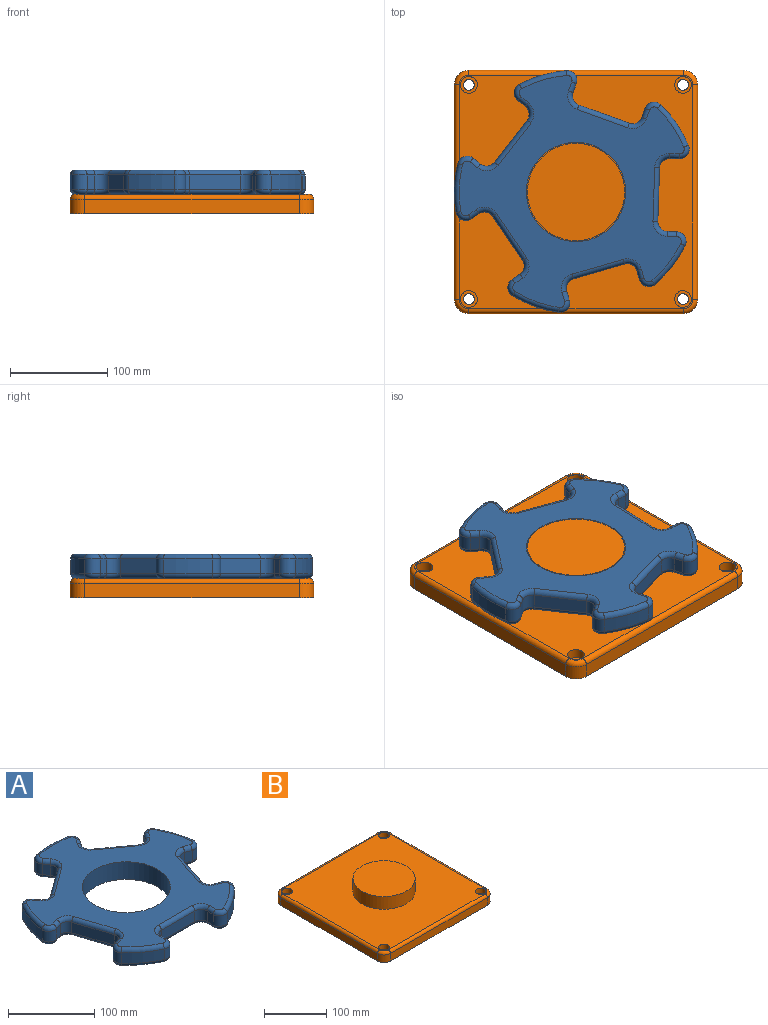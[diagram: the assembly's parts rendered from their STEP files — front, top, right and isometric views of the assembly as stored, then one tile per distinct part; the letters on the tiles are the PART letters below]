
ASSEMBLY  parts=2 mates=1
PART A: 123 faces, bbox 268.9x258.5x25 mm
  f0: plane 238.57x229.73mm, normal (0,0,1), area 21505.7mm2, adj f6,f43,f44,f45,f46,f47,f48,f49
  f1: plane 238.57x229.73mm, normal (0,0,-1), area 21505.7mm2, adj f6,f83,f84,f85,f86,f87,f88,f89
  f2: cylinder r=125mm len=40.68mm, axis (0,0,-1), area 759.5mm2, adj f13,f42,f51,f91
  f3: cylinder r=125mm len=47.82mm, axis (0,0,-1), area 759.5mm2, adj f35,f41,f67,f107
  f4: cylinder r=125mm len=50.29mm, axis (0,0,-1), area 759.5mm2, adj f28,f34,f82,f122
  f5: cylinder r=125mm len=47.82mm, axis (0,0,-1), area 759.5mm2, adj f21,f27,f66,f106
  f6: cylinder r=51mm len=102mm, axis (0,0,-1), area 8011.1mm2, adj f0,f1
  f7: cylinder r=125mm len=40.68mm, axis (0,0,-1), area 759.5mm2, adj f14,f20,f50,f90
  f8: plane 15x9.73mm, normal (-1,0,0), area 146mm2, adj f11,f14,f46,f86
  f9: plane 55x15mm, normal (0,-1,0), area 825mm2, adj f11,f12,f43,f83
  f10: plane 15x9.73mm, normal (1,0,0), area 146mm2, adj f12,f13,f47,f87
  f11: cylinder r=10mm len=15mm, axis (0,0,-1), area 235.6mm2, adj f8,f9,f44,f84
  f12: cylinder r=10mm len=15mm, axis (0,0,-1), area 235.6mm2, adj f9,f10,f45,f85
  f13: cylinder r=10mm len=15mm, axis (0,0,-1), area 299.5mm2, adj f2,f10,f49,f89
  f14: cylinder r=10mm len=15mm, axis (0,0,-1), area 299.5mm2, adj f7,f8,f48,f88
  f15: plane 15x9.26mm, normal (-0.31,-0.95,0), area 146mm2, adj f18,f21,f62,f102
  f16: plane 52.31x17mm, normal (0.95,-0.31,0), area 825mm2, adj f18,f19,f58,f98
  f17: plane 15x9.26mm, normal (0.31,0.95,0), area 146mm2, adj f19,f20,f54,f94
  f18: cylinder r=10mm len=15mm, axis (0,0,-1), area 235.6mm2, adj f15,f16,f60,f100
  f19: cylinder r=10mm len=15mm, axis (0,0,-1), area 235.6mm2, adj f16,f17,f56,f96
  f20: cylinder r=10mm len=16.25mm, axis (0,0,-1), area 299.5mm2, adj f7,f17,f52,f92
  f21: cylinder r=10mm len=15mm, axis (0,0,-1), area 299.5mm2, adj f5,f15,f64,f104
  f22: plane 15x7.87mm, normal (0.81,-0.59,0), area 146mm2, adj f25,f28,f78,f118
  f23: plane 44.5x32.33mm, normal (0.59,0.81,0), area 825mm2, adj f25,f26,f74,f114
  f24: plane 15x7.87mm, normal (-0.81,0.59,0), area 146mm2, adj f26,f27,f70,f110
  f25: cylinder r=10mm len=15mm, axis (0,0,-1), area 235.6mm2, adj f22,f23,f76,f116
  f26: cylinder r=10mm len=15mm, axis (0,0,-1), area 235.6mm2, adj f23,f24,f72,f112
  f27: cylinder r=10mm len=16.78mm, axis (0,0,-1), area 299.5mm2, adj f5,f24,f68,f108
  f28: cylinder r=10mm len=15.67mm, axis (0,0,-1), area 299.5mm2, adj f4,f22,f80,f120
  f29: plane 15x7.87mm, normal (0.81,0.59,0), area 146mm2, adj f32,f35,f71,f111
  f30: plane 44.5x32.33mm, normal (-0.59,0.81,0), area 825mm2, adj f32,f33,f75,f115
  f31: plane 15x7.87mm, normal (-0.81,-0.59,0), area 146mm2, adj f33,f34,f79,f119
  f32: cylinder r=10mm len=15mm, axis (0,0,-1), area 235.6mm2, adj f29,f30,f73,f113
  f33: cylinder r=10mm len=15mm, axis (0,0,-1), area 235.6mm2, adj f30,f31,f77,f117
  f34: cylinder r=10mm len=15.67mm, axis (0,0,-1), area 299.5mm2, adj f4,f31,f81,f121
  f35: cylinder r=10mm len=16.78mm, axis (0,0,-1), area 299.5mm2, adj f3,f29,f69,f109
  f36: plane 15x9.26mm, normal (-0.31,0.95,0), area 146mm2, adj f39,f42,f55,f95
  f37: plane 52.31x17mm, normal (-0.95,-0.31,0), area 825mm2, adj f39,f40,f59,f99
  f38: plane 15x9.26mm, normal (0.31,-0.95,0), area 146mm2, adj f40,f41,f63,f103
  f39: cylinder r=10mm len=15mm, axis (0,0,-1), area 235.6mm2, adj f36,f37,f57,f97
  f40: cylinder r=10mm len=15mm, axis (0,0,-1), area 235.6mm2, adj f37,f38,f61,f101
  f41: cylinder r=10mm len=15mm, axis (0,0,-1), area 299.5mm2, adj f3,f38,f65,f105
  f42: cylinder r=10mm len=16.25mm, axis (0,0,-1), area 299.5mm2, adj f2,f36,f53,f93
  f43: cylinder r=5mm len=55mm, axis (1,0,0), area 432mm2, adj f0,f9,f44,f45
  f44: torus R=15mm, axis (0,0,1), area 145.8mm2, adj f0,f11,f43,f46
  f45: torus R=15mm, axis (0,0,1), area 145.8mm2, adj f0,f12,f43,f47
  f46: cylinder r=5mm len=9.73mm, axis (0,-1,0), area 76.4mm2, adj f0,f8,f44,f48
  f47: cylinder r=5mm len=9.73mm, axis (0,1,0), area 76.4mm2, adj f0,f10,f45,f49
  f48: torus R=5mm, axis (0,0,1), area 128.3mm2, adj f0,f14,f46,f50
  f49: torus R=5mm, axis (0,0,1), area 128.3mm2, adj f0,f13,f47,f51
  f50: torus R=120mm, axis (0,0,1), area 391.9mm2, adj f0,f7,f48,f52
  f51: torus R=120mm, axis (0,0,1), area 391.9mm2, adj f0,f2,f49,f53
  f52: torus R=5mm, axis (0,0,1), area 128.3mm2, adj f0,f20,f50,f54
  f53: torus R=5mm, axis (0,0,1), area 128.3mm2, adj f0,f42,f51,f55
  f54: cylinder r=5mm len=10.8mm, axis (-0.95,0.31,0), area 76.4mm2, adj f0,f17,f52,f56
  f55: cylinder r=5mm len=10.8mm, axis (-0.95,-0.31,0), area 76.4mm2, adj f0,f36,f53,f57
  f56: torus R=15mm, axis (0,0,1), area 145.8mm2, adj f0,f19,f54,f58
  f57: torus R=15mm, axis (0,0,1), area 145.8mm2, adj f0,f39,f55,f59
  f58: cylinder r=5mm len=53.85mm, axis (0.31,0.95,0), area 432mm2, adj f0,f16,f56,f60
  f59: cylinder r=5mm len=53.85mm, axis (0.31,-0.95,0), area 432mm2, adj f0,f37,f57,f61
  f60: torus R=15mm, axis (0,0,1), area 145.8mm2, adj f0,f18,f58,f62
  f61: torus R=15mm, axis (0,0,1), area 145.8mm2, adj f0,f40,f59,f63
  f62: cylinder r=5mm len=10.8mm, axis (0.95,-0.31,0), area 76.4mm2, adj f0,f15,f60,f64
  f63: cylinder r=5mm len=10.8mm, axis (0.95,0.31,0), area 76.4mm2, adj f0,f38,f61,f65
  f64: torus R=5mm, axis (0,0,1), area 128.3mm2, adj f0,f21,f62,f66
  f65: torus R=5mm, axis (0,0,1), area 128.3mm2, adj f0,f41,f63,f67
  f66: torus R=120mm, axis (0,0,1), area 391.9mm2, adj f0,f5,f64,f68
  f67: torus R=120mm, axis (0,0,1), area 391.9mm2, adj f0,f3,f65,f69
  f68: torus R=5mm, axis (0,0,1), area 128.3mm2, adj f0,f27,f66,f70
  f69: torus R=5mm, axis (0,0,1), area 128.3mm2, adj f0,f35,f67,f71
  f70: cylinder r=5mm len=10.81mm, axis (-0.59,-0.81,0), area 76.4mm2, adj f0,f24,f68,f72
  f71: cylinder r=5mm len=10.81mm, axis (-0.59,0.81,0), area 76.4mm2, adj f0,f29,f69,f73
  f72: torus R=15mm, axis (0,0,1), area 145.8mm2, adj f0,f26,f70,f74
  f73: torus R=15mm, axis (0,0,1), area 145.8mm2, adj f0,f32,f71,f75
  f74: cylinder r=5mm len=47.44mm, axis (-0.81,0.59,0), area 432mm2, adj f0,f23,f72,f76
  f75: cylinder r=5mm len=47.44mm, axis (-0.81,-0.59,0), area 432mm2, adj f0,f30,f73,f77
  f76: torus R=15mm, axis (0,0,1), area 145.8mm2, adj f0,f25,f74,f78
  f77: torus R=15mm, axis (0,0,1), area 145.8mm2, adj f0,f33,f75,f79
  f78: cylinder r=5mm len=10.81mm, axis (0.59,0.81,0), area 76.4mm2, adj f0,f22,f76,f80
  f79: cylinder r=5mm len=10.81mm, axis (0.59,-0.81,0), area 76.4mm2, adj f0,f31,f77,f81
  f80: torus R=5mm, axis (0,0,1), area 128.3mm2, adj f0,f28,f78,f82
  f81: torus R=5mm, axis (0,0,1), area 128.3mm2, adj f0,f34,f79,f82
  f82: torus R=120mm, axis (0,0,1), area 391.9mm2, adj f0,f4,f80,f81
  f83: cylinder r=5mm len=55mm, axis (-1,0,0), area 432mm2, adj f1,f9,f84,f85
  f84: torus R=15mm, axis (0,0,1), area 145.8mm2, adj f1,f11,f83,f86
  f85: torus R=15mm, axis (0,0,1), area 145.8mm2, adj f1,f12,f83,f87
  f86: cylinder r=5mm len=9.73mm, axis (0,1,0), area 76.4mm2, adj f1,f8,f84,f88
  f87: cylinder r=5mm len=9.73mm, axis (0,-1,0), area 76.4mm2, adj f1,f10,f85,f89
  f88: torus R=5mm, axis (0,0,1), area 128.3mm2, adj f1,f14,f86,f90
  f89: torus R=5mm, axis (0,0,1), area 128.3mm2, adj f1,f13,f87,f91
  f90: torus R=120mm, axis (0,0,1), area 391.9mm2, adj f1,f7,f88,f92
  f91: torus R=120mm, axis (0,0,1), area 391.9mm2, adj f1,f2,f89,f93
  f92: torus R=5mm, axis (0,0,1), area 128.3mm2, adj f1,f20,f90,f94
  f93: torus R=5mm, axis (0,0,1), area 128.3mm2, adj f1,f42,f91,f95
  f94: cylinder r=5mm len=10.8mm, axis (0.95,-0.31,0), area 76.4mm2, adj f1,f17,f92,f96
  f95: cylinder r=5mm len=10.8mm, axis (0.95,0.31,0), area 76.4mm2, adj f1,f36,f93,f97
  f96: torus R=15mm, axis (0,0,1), area 145.8mm2, adj f1,f19,f94,f98
  f97: torus R=15mm, axis (0,0,1), area 145.8mm2, adj f1,f39,f95,f99
  f98: cylinder r=5mm len=53.85mm, axis (-0.31,-0.95,0), area 432mm2, adj f1,f16,f96,f100
  f99: cylinder r=5mm len=53.85mm, axis (-0.31,0.95,0), area 432mm2, adj f1,f37,f97,f101
  f100: torus R=15mm, axis (0,0,1), area 145.8mm2, adj f1,f18,f98,f102
  f101: torus R=15mm, axis (0,0,1), area 145.8mm2, adj f1,f40,f99,f103
  f102: cylinder r=5mm len=10.8mm, axis (-0.95,0.31,0), area 76.4mm2, adj f1,f15,f100,f104
  f103: cylinder r=5mm len=10.8mm, axis (-0.95,-0.31,0), area 76.4mm2, adj f1,f38,f101,f105
  f104: torus R=5mm, axis (0,0,1), area 128.3mm2, adj f1,f21,f102,f106
  f105: torus R=5mm, axis (0,0,1), area 128.3mm2, adj f1,f41,f103,f107
  f106: torus R=120mm, axis (0,0,1), area 391.9mm2, adj f1,f5,f104,f108
  f107: torus R=120mm, axis (0,0,1), area 391.9mm2, adj f1,f3,f105,f109
  f108: torus R=5mm, axis (0,0,1), area 128.3mm2, adj f1,f27,f106,f110
  f109: torus R=5mm, axis (0,0,1), area 128.3mm2, adj f1,f35,f107,f111
  f110: cylinder r=5mm len=10.81mm, axis (0.59,0.81,0), area 76.4mm2, adj f1,f24,f108,f112
  f111: cylinder r=5mm len=10.81mm, axis (0.59,-0.81,0), area 76.4mm2, adj f1,f29,f109,f113
  f112: torus R=15mm, axis (0,0,1), area 145.8mm2, adj f1,f26,f110,f114
  f113: torus R=15mm, axis (0,0,1), area 145.8mm2, adj f1,f32,f111,f115
  f114: cylinder r=5mm len=47.44mm, axis (0.81,-0.59,0), area 432mm2, adj f1,f23,f112,f116
  f115: cylinder r=5mm len=47.44mm, axis (0.81,0.59,0), area 432mm2, adj f1,f30,f113,f117
  f116: torus R=15mm, axis (0,0,1), area 145.8mm2, adj f1,f25,f114,f118
  f117: torus R=15mm, axis (0,0,1), area 145.8mm2, adj f1,f33,f115,f119
  f118: cylinder r=5mm len=10.81mm, axis (-0.59,-0.81,0), area 76.4mm2, adj f1,f22,f116,f120
  f119: cylinder r=5mm len=10.81mm, axis (-0.59,0.81,0), area 76.4mm2, adj f1,f31,f117,f121
  f120: torus R=5mm, axis (0,0,1), area 128.3mm2, adj f1,f28,f118,f122
  f121: torus R=5mm, axis (0,0,1), area 128.3mm2, adj f1,f34,f119,f122
  f122: torus R=120mm, axis (0,0,1), area 391.9mm2, adj f1,f4,f120,f121
PART B: 32 faces, bbox 252.5x252.5x45 mm
  f0: plane 220x15mm, normal (1,0,0), area 3300mm2, adj f5,f8,f11,f27
  f1: plane 220x15mm, normal (0,1,0), area 3300mm2, adj f5,f8,f9,f31
  f2: plane 220x15mm, normal (-1,0,0), area 3300mm2, adj f5,f9,f10,f28
  f3: plane 220x15mm, normal (0,-1,0), area 3300mm2, adj f5,f10,f11,f24
  f4: plane 240x240mm, normal (0,0,1), area 48725.4mm2, adj f6,f14,f17,f20,f23,f24,f25,f26
  f5: plane 250x250mm, normal (0,0,-1), area 61926.7mm2, adj f0,f1,f2,f3,f8,f9,f10,f11
  f6: cylinder r=50mm len=100mm, axis (0,0,-1), area 7854mm2, adj f4,f7
  f7: plane 100x100mm, normal (0,0,1), area 7854mm2, adj f6
  f8: cylinder r=15mm len=15mm, axis (0,0,-1), area 353.4mm2, adj f0,f1,f5,f29
  f9: cylinder r=15mm len=15mm, axis (0,0,1), area 353.4mm2, adj f1,f2,f5,f30
  f10: cylinder r=15mm len=15mm, axis (0,0,-1), area 353.4mm2, adj f2,f3,f5,f26
  f11: cylinder r=15mm len=15mm, axis (0,0,1), area 353.4mm2, adj f0,f3,f5,f25
  f12: cylinder r=5.5mm len=11mm, axis (0,0,1), area 345.6mm2, adj f5,f13
  f13: plane 17.25x17.25mm, normal (0,0,1), area 138.7mm2, adj f12,f14
  f14: cylinder r=8.62mm len=17.25mm, axis (0,0,1), area 541.9mm2, adj f4,f13
  f15: cylinder r=5.5mm len=11mm, axis (0,0,1), area 345.6mm2, adj f5,f16
  f16: plane 17.25x17.25mm, normal (0,0,1), area 138.7mm2, adj f15,f17
  f17: cylinder r=8.62mm len=17.25mm, axis (0,0,1), area 541.9mm2, adj f4,f16
  f18: cylinder r=5.5mm len=11mm, axis (0,0,1), area 345.6mm2, adj f5,f19
  f19: plane 17.25x17.25mm, normal (0,0,1), area 138.7mm2, adj f18,f20
  f20: cylinder r=8.62mm len=17.25mm, axis (0,0,1), area 541.9mm2, adj f4,f19
  f21: cylinder r=5.5mm len=11mm, axis (0,0,1), area 345.6mm2, adj f5,f22
  f22: plane 17.25x17.25mm, normal (0,0,1), area 138.7mm2, adj f21,f23
  f23: cylinder r=8.62mm len=17.25mm, axis (0,0,1), area 541.9mm2, adj f4,f22
  f24: cylinder r=5mm len=220mm, axis (-1,0,0), area 1727.9mm2, adj f3,f4,f25,f26
  f25: torus R=10mm, axis (0,0,1), area 162.6mm2, adj f4,f11,f24,f27
  f26: torus R=10mm, axis (0,0,1), area 162.6mm2, adj f4,f10,f24,f28
  f27: cylinder r=5mm len=220mm, axis (0,-1,0), area 1727.9mm2, adj f0,f4,f25,f29
  f28: cylinder r=5mm len=220mm, axis (0,1,0), area 1727.9mm2, adj f2,f4,f26,f30
  f29: torus R=10mm, axis (0,0,1), area 162.6mm2, adj f4,f8,f27,f31
  f30: torus R=10mm, axis (0,0,1), area 162.6mm2, adj f4,f9,f28,f31
  f31: cylinder r=5mm len=220mm, axis (1,0,0), area 1727.9mm2, adj f1,f4,f29,f30
PLACE A rot(axis=(0,0,1),16.1deg) t=(0,0,0)mm
PLACE B at identity fixed
MATE revolute A.f2 <-> B.f6  axis (0,0,1) through (0,0,45)mm
